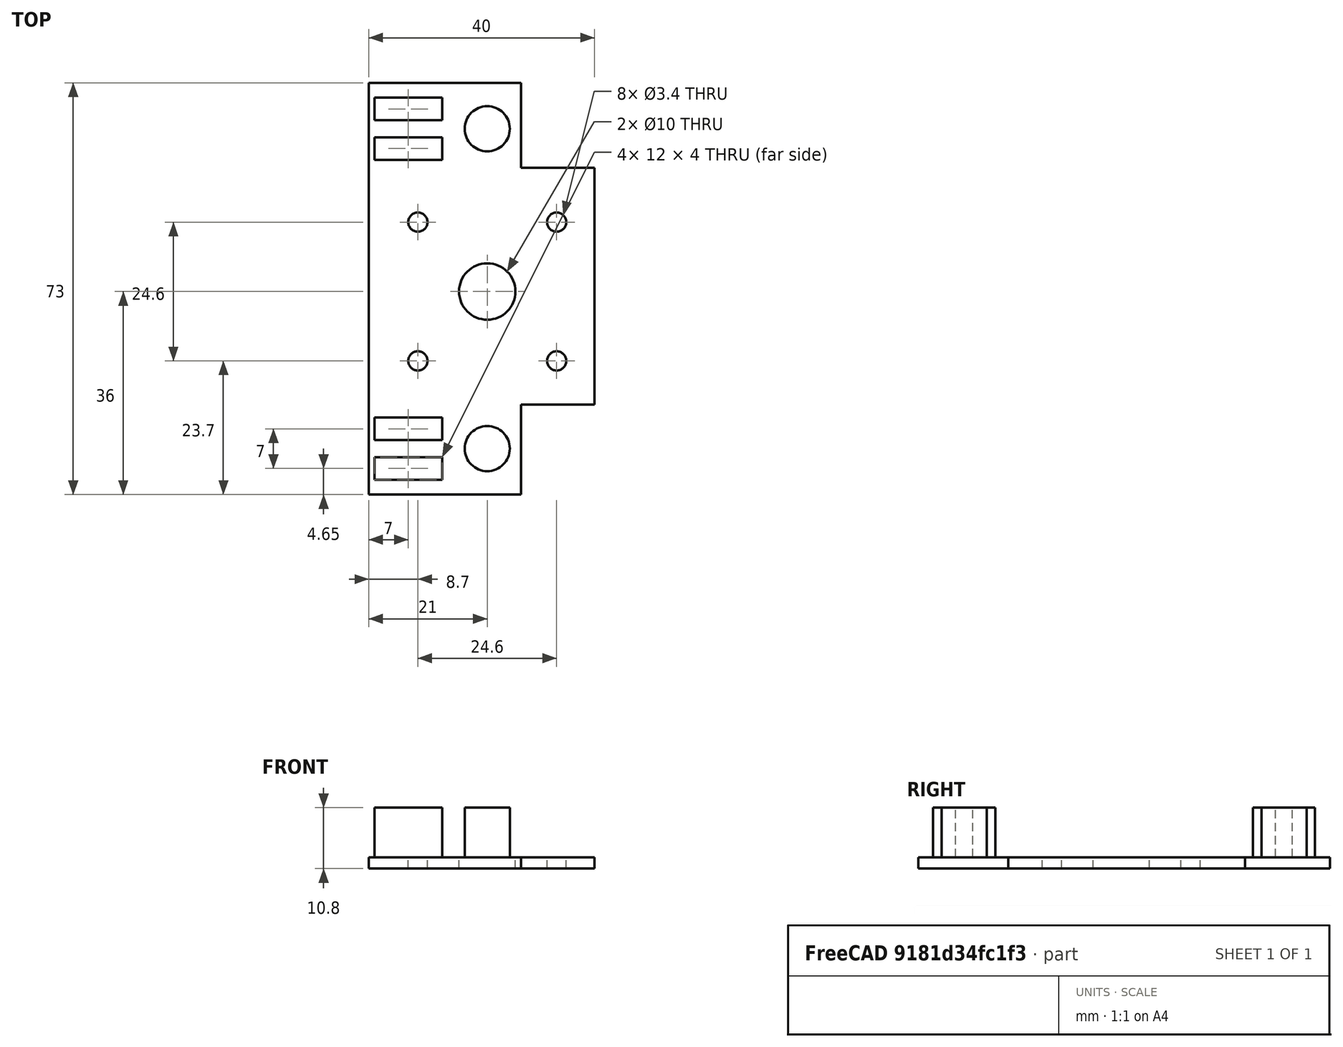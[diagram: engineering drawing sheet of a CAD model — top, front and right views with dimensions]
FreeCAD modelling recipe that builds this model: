
FCSTD DOCUMENT  (FreeCAD 0.16R6712 (Git))
Label: Soportecorreas
License: All rights reserved
LicenseURL: http://en.wikipedia.org/wiki/All_rights_reserved
objects: Part::Box×4, Part::Cylinder×3, Part::MultiFuse×3, Part::FeaturePython×2, Part::Cut×2, Part::Feature×1
note: 15 computed .brp shape members not serialized (recipe doc carries the construction recipe); baked Part::Feature solids carry a one-line shape summary decoded from their .brp

FEATURE [Part::Box] Box  label="Cubo"
  Height = 2
  Length = 27
  Width = 73
FEATURE [Part::Box] Box001  label="Cubo001"
  Height = 2
  Length = 40
  Placement = pos=(0,15.96,0) rot=(0,0,1;0rad)
  Width = 41.96
FEATURE [Part::Cylinder] Cylinder  label="Cilindro"
  Angle = 360
  Height = 2
  Placement = pos=(8.7,23.7,0) rot=(0,0,1;0rad)
  Radius = 1.7
FEATURE [Part::FeaturePython] Array  # Draft array (typed FeaturePython)
  Angle = 360
  ArrayType = 0
  Axis = (0,0,1)
  Base = -> Cylinder
  Center = (0,0,0)
  Fuse = false
  IntervalAxis = (0,0,0)
  IntervalX = (24.6,0,0)
  IntervalY = (0,24.6,0)
  IntervalZ = (0,0,0)
  NumberPolar = 1
  NumberX = 2
  NumberY = 2
  NumberZ = 1
FEATURE [Part::Cylinder] Cylinder001  label="Cilindro001"
  Angle = 360
  Height = 2
  Placement = pos=(21,36,0) rot=(0,0,1;0rad)
  Radius = 5
FEATURE [Part::MultiFuse] Fusion
  Shapes = -> [Box,Box001]
FEATURE [Part::Cut] Cut
  Base = -> Fusion
  Tool = -> Cylinder001
FEATURE [Part::Cut] Cut001
  Base = -> Cut
  Tool = -> Array
FEATURE [Part::Box] Box002  label="Cubo002"
  Height = 8.8
  Length = 12
  Placement = pos=(1,2.65,2) rot=(0,0,1;0rad)
  Width = 4
FEATURE [Part::Box] Box003  label="Cubo003"
  Height = 8.8
  Length = 12
  Placement = pos=(1,9.65,2) rot=(0,0,1;0rad)
  Width = 4
FEATURE [Part::Cylinder] Cylinder002  label="Cilindro002"
  Angle = 360
  Height = 8.8
  Placement = pos=(21,8.15,2) rot=(0,0,1;0rad)
  Radius = 4
FEATURE [Part::MultiFuse] Fusion001
  Shapes = -> [Box003,Box002,Cylinder002]
FEATURE [Part::FeaturePython] Array001  # Draft array (typed FeaturePython)
  Angle = 360
  ArrayType = 0
  Axis = (0,0,1)
  Base = -> Fusion001
  Center = (0,0,0)
  Fuse = false
  IntervalAxis = (0,0,0)
  IntervalX = (1,0,0)
  IntervalY = (0,56.7,0)
  IntervalZ = (0,0,0)
  NumberPolar = 1
  NumberX = 1
  NumberY = 2
  NumberZ = 1
FEATURE [Part::MultiFuse] Fusion002
  Shapes = -> [Array001,Cut001]
FEATURE [Part::Feature] Fusion002001  label="Fusion003"
  shape: bbox 40 x 73 x 10.8 mm, 39 faces (baked)
